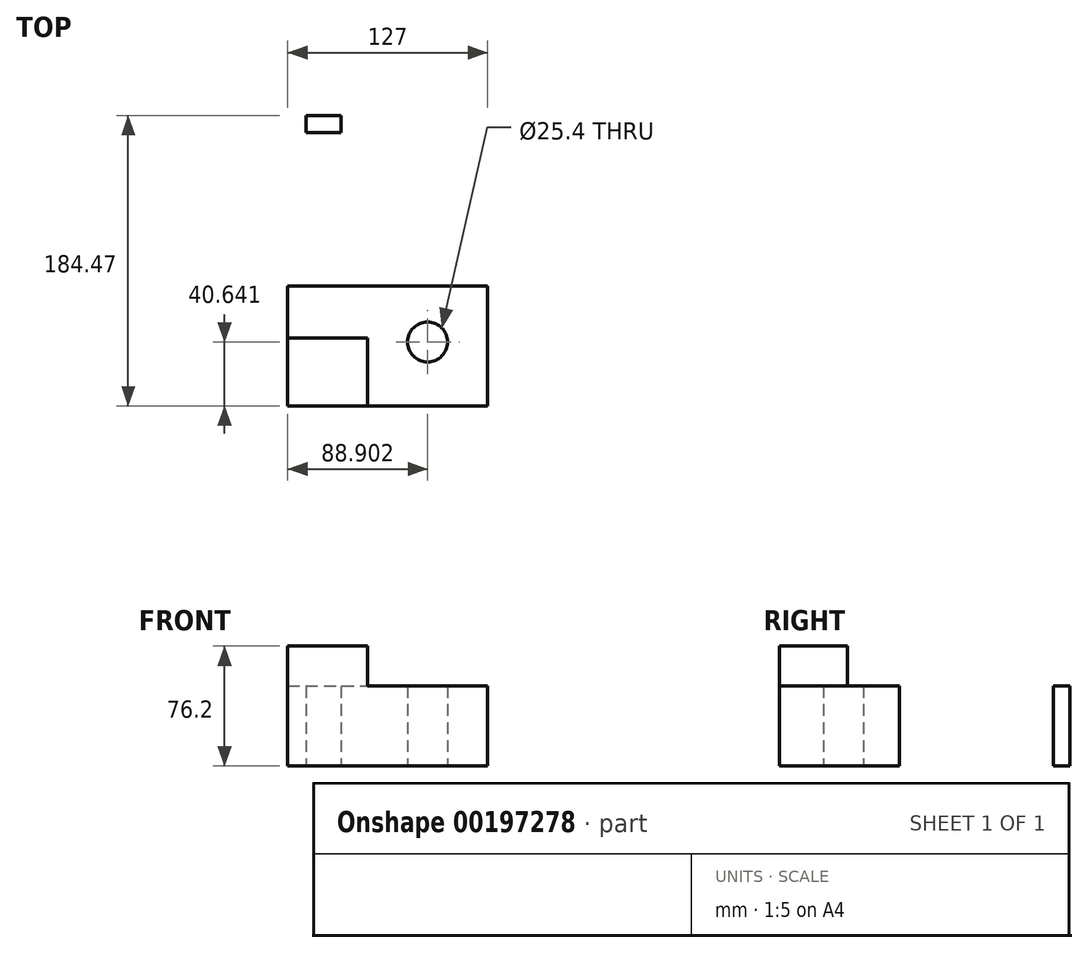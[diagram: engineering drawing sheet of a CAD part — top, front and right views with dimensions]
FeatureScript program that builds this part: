
annotation { "Feature Type Name" : "Feature", "Feature Type Description" : "" }
export const myFeature = defineFeature(function(context is Context, id is Id, definition is map)
    precondition{}
    {
        {
            var Q0;
            Q0=qCreatedBy(makeId("Top.planeOp"),FACE);
            var sketch = newSketch(context, id + "F0", { "sketchPlane" : qUnion([Q0])});
            skLineSegment(sketch, "E0.bottom", {"start": v(-209.28, 16.82) * mm, "end": v(-82.28, 16.82) * mm});
            skLineSegment(sketch, "E0.top", {"start": v(-209.28, -59.38) * mm, "end": v(-82.28, -59.38) * mm});
            skLineSegment(sketch, "E0.left", {"start": v(-209.28, 16.82) * mm, "end": v(-209.28, -59.38) * mm});
            skLineSegment(sketch, "E0.right", {"start": v(-82.28, 16.82) * mm, "end": v(-82.28, -59.38) * mm});
            skCircle(sketch, "E1", {"center": v(-120.38, -18.74) * mm, "radius": 12.7 * mm});
            skLineSegment(sketch, "E2", {"start": v(-82.28, -59.38) * mm, "end": v(-209.28, 16.82) * mm, "construction": true});
            skLineSegment(sketch, "E3.bottom", {"start": v(-209.28, 93.25) * mm, "end": v(-160.08, 93.25) * mm, "construction": true});
            skLineSegment(sketch, "E3.top", {"start": v(-209.28, 42.22) * mm, "end": v(-160.08, 42.22) * mm, "construction": true});
            skLineSegment(sketch, "E3.left", {"start": v(-209.28, 93.25) * mm, "end": v(-209.28, 42.22) * mm, "construction": true});
            skLineSegment(sketch, "E3.right", {"start": v(-160.08, 93.25) * mm, "end": v(-160.08, 42.22) * mm, "construction": true});
            skLineSegment(sketch, "E4.bottom", {"start": v(-197.7, 125.09) * mm, "end": v(-175.5, 125.09) * mm});
            skLineSegment(sketch, "E4.top", {"start": v(-197.7, 114.4) * mm, "end": v(-175.5, 114.4) * mm});
            skLineSegment(sketch, "E4.left", {"start": v(-197.7, 125.09) * mm, "end": v(-197.7, 114.4) * mm});
            skLineSegment(sketch, "E4.right", {"start": v(-175.5, 125.09) * mm, "end": v(-175.5, 114.4) * mm});
            skPoint(sketch, "E5", {"position": v(-145.78, -21.28) * mm});
            skSolve(sketch);
        }
        {
            var Q0;
            Q0 = qSketchRegion(id + "F0", true);
            extrude(context, id + "F1", {"entities" : qUnion([Q0]), "depth" : 50.8 * mm});
        }
        {
            var Q0;
            Q0=makeQuery(id+"F1.opExtrude","CAP_FACE",FACE,{"disambiguationData":[OSD([sQuery(id+"F0.wireOp",EDGE,"E0.bottom"),sQuery(id+"F0.wireOp",EDGE,"E0.top"),sQuery(id+"F0.wireOp",EDGE,"E0.left"),sQuery(id+"F0.wireOp",EDGE,"E0.right"),sQuery(id+"F0.wireOp",EDGE,"E1")])],"isStart":false});
            var sketch = newSketch(context, id + "F2", { "sketchPlane" : qUnion([Q0])});
            skLineSegment(sketch, "E6.bottom", {"start": v(-209.28, -59.38) * mm, "end": v(-158.48, -59.38) * mm});
            skLineSegment(sketch, "E6.top", {"start": v(-209.28, -16.2) * mm, "end": v(-158.48, -16.2) * mm});
            skLineSegment(sketch, "E6.left", {"start": v(-209.28, -59.38) * mm, "end": v(-209.28, -16.2) * mm});
            skLineSegment(sketch, "E6.right", {"start": v(-158.48, -59.38) * mm, "end": v(-158.48, -16.2) * mm});
            skSolve(sketch);
        }
        {
            var Q0;
            Q0 = qSketchRegion(id + "F2", true);
            extrude(context, id + "F3", {"entities" : qUnion([Q0]), "operationType" : NewBodyOperationType.ADD, "depth" : 25.4 * mm});
        }
    });
